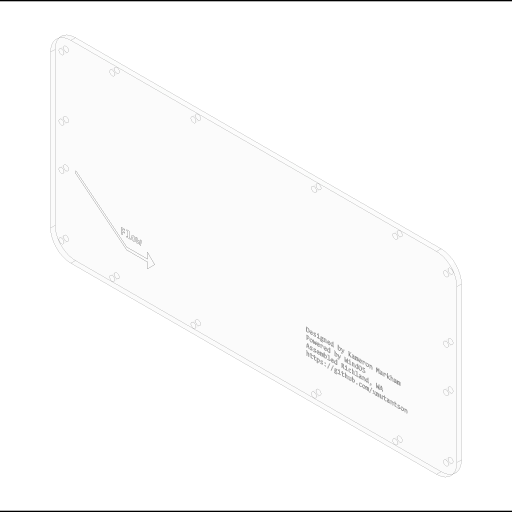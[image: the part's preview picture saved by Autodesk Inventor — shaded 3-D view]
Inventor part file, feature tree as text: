
AUTODESK INVENTOR PART (.ipt)
format: ipt  version: 2023 (Build 270158000, 158)  size: 1,887,232 bytes
history: native  units: in
note: dims shown in document units (in); Inventor stores cm internally (conversion verified against a paired STEP export)
features: extrude x3, sketch x3
ambient origin geometry x8: Origin, YZ Plane, XZ Plane, XY Plane, X Axis, Y Axis, Z Axis, Center Point
bodies: Solid1 (feature_tree)
feature tree (6):
  extrude  "Extrusion1"  Depth=9.5in
  extrude  "Extrusion2"  Depth=0.227in TaperAngle=0.0deg
  extrude  "Extrusion3"  Depth=0.535in
  sketch  "Sketch1"  dims[d0=20.0in d1=9.5in]
  sketch  "Sketch2"  dims[d2=1.0in d3=0.227in d4=0.0in]
  sketch  "Sketch3"  dims[d5=0.25in d6=0.535in d7=0.72in d8=0.25in d9=3.0in d10=0.535in d11=0.25in d12=2.061in d13=0.535in d14=0.25in d15=3.0in d16=0.535in d17=0.7874in d19=18.931in d20=0.3937in d22=1.0in d24=0.25in d25=2.5in d26=0.35in d27=0.25in d28=4.0in d29=0.25in d30=5.931in d31=0.25in d32=4.0in d33=0.37in d34=0.37in d35=0.37in d36=0.7874in d38=8.761in d39=0.3937in d41=1.0in d43=0.0in d44=0.0in d45=1.25in d46=3.75in d47=4.0in d48=2.0in d49=1.375in d50=45.0deg d51=0.7075in d55=0.0625in d56=0.0625in d57=0.05in d58=0.05in d59=0.0in d60=0.001in d61=0.0in]
